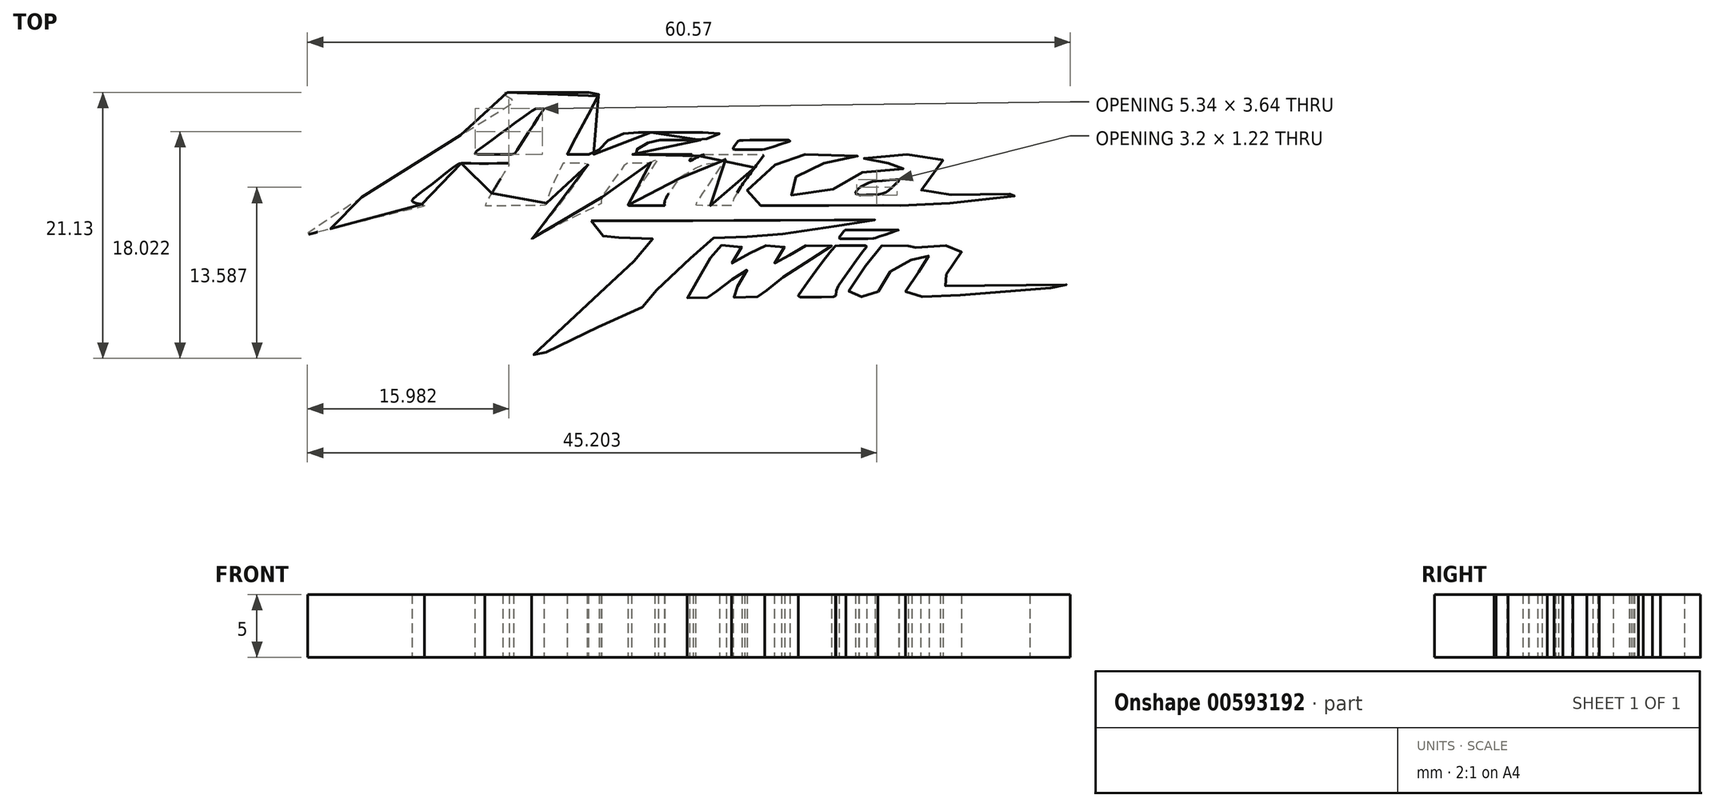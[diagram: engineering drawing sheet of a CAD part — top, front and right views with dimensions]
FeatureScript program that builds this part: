
annotation { "Feature Type Name" : "Feature", "Feature Type Description" : "" }
export const myFeature = defineFeature(function(context is Context, id is Id, definition is map)
    precondition{}
    {
        {
            var Q0;
            Q0=qCreatedBy(makeId("Top.planeOp"),FACE);
            var sketch = newSketch(context, id + "F0", { "sketchPlane" : qUnion([Q0])});
            skFitSpline(sketch, "E0", {"points": [v(-31.44, 20.71) * mm, v(-28.3, 20.77) * mm, v(-24.77, 20.79) * mm, v(-21.15, 20.83) * mm, v(-17.69, 20.85) * mm, v(-13.86, 20.87) * mm, v(-10.72, 20.85) * mm, v(-9.64, 20.77) * mm, v(-9.44, 20.67) * mm, v(-9.36, 20.45) * mm, v(-9.71, 19.84) * mm, v(-10.66, 17.85) * mm, v(-11.86, 15.37) * mm, v(-12.62, 13.83) * mm, v(-12.87, 13.46) * mm, v(-12.36, 13.66) * mm, v(-10.48, 14.38) * mm, v(-9.76, 14.62) * mm, v(-8.3, 14.67) * mm, v(-0.15, 14.62) * mm, v(8.5, 14.6) * mm, v(10.43, 14.62) * mm, v(10.86, 14.5) * mm, v(10.52, 14.24) * mm, v(9.13, 13.52) * mm, v(8.62, 13.24) * mm, v(9.3, 13.23) * mm, v(13.38, 13.2) * mm, v(17.6, 13.21) * mm, v(21.22, 13.2) * mm, v(22.36, 13.21) * mm, v(22.72, 13.17) * mm, v(22.9, 13.05) * mm, v(22.8, 12.92) * mm, v(22, 12.5) * mm, v(19.52, 11.38) * mm, v(19.17, 11.22) * mm, v(19.52, 11.18) * mm, v(21.42, 11.2) * mm, v(27.58, 11.15) * mm, v(35.7, 11.2) * mm, v(39.4, 11.2) * mm, v(39.96, 11.2) * mm, v(40.45, 11.02) * mm, v(41.07, 10.67) * mm, v(43.51, 8.93) * mm, v(43.88, 8.62) * mm, v(44.1, 8.35) * mm, v(44.07, 8.16) * mm, v(43.88, 7.78) * mm, v(43.2, 6.82) * mm, v(41.7, 4.75) * mm, v(41.4, 4.44) * mm, v(41.8, 4.44) * mm, v(46.51, 4.34) * mm, v(54.03, 4.15) * mm, v(62.87, 3.9) * mm, v(63.5, 3.86) * mm, v(63.75, 3.7) * mm, v(63.8, 3.5) * mm, v(63.56, 3.27) * mm, v(62.78, 3.02) * mm, v(61.33, 2.68) * mm, v(50.17, 0.51) * mm, v(48.29, 0.16) * mm, v(43.82, -0.7) * mm, v(41.17, -1.17) * mm, v(40.71, -1.31) * mm, v(40.3, -1.52) * mm, v(38.4, -2.7) * mm, v(38.08, -2.95) * mm, v(38.48, -2.96) * mm, v(42.95, -2.96) * mm, v(43.87, -3) * mm, v(44.42, -3.15) * mm, v(45.17, -3.73) * mm, v(47.66, -5.83) * mm, v(47.85, -6) * mm, v(47.88, -6.2) * mm, v(47.65, -6.53) * mm, v(45.18, -9.97) * mm, v(44.95, -10.32) * mm, v(45.44, -10.34) * mm, v(49.6, -10.42) * mm, v(60.85, -10.66) * mm, v(68.92, -10.88) * mm, v(69.35, -10.9) * mm, v(69.58, -11.06) * mm, v(69.63, -11.3) * mm, v(69.4, -11.5) * mm, v(68.72, -11.77) * mm, v(67.84, -11.94) * mm, v(61.37, -13.03) * mm, v(54.69, -13.9) * mm, v(46.25, -14.7) * mm, v(39.74, -15.1) * mm, v(35.06, -15.2) * mm, v(29.92, -15.28) * mm, v(24.8, -15.36) * mm, v(22.23, -15.43) * mm, v(14.78, -15.56) * mm, v(7.73, -15.76) * mm, v(1.76, -15.96) * mm, v(-0.16, -16.08) * mm, v(-1.23, -16.17) * mm, v(-1.7, -16.22) * mm, v(-2.2, -16.36) * mm, v(-3.15, -16.73) * mm, v(-5.36, -17.68) * mm, v(-8.55, -19) * mm, v(-11.16, -20.13) * mm, v(-15.96, -22.24) * mm, v(-19.22, -23.72) * mm, v(-24.73, -26.23) * mm, v(-29.57, -28.5) * mm, v(-31.83, -29.52) * mm, v(-33.6, -30.36) * mm, v(-33.79, -30.44) * mm, v(-33.93, -30.42) * mm, v(-34.06, -30.3) * mm, v(-34.08, -30.09) * mm, v(-33.96, -29.86) * mm, v(-33.08, -28.95) * mm, v(-30.44, -26.24) * mm, v(-27.52, -23.44) * mm, v(-24.82, -20.86) * mm, v(-21.12, -17.38) * mm, v(-17.92, -14.4) * mm, v(-14.38, -11.08) * mm, v(-11, -7.9) * mm, v(-9.75, -6.67) * mm, v(-9.62, -6.52) * mm, v(-9.85, -6.53) * mm, v(-10.86, -6.51) * mm, v(-10.98, -6.5) * mm, v(-11.63, -6.92) * mm, v(-11.95, -7.17) * mm, v(-12.1, -7.28) * mm, v(-12.24, -7.26) * mm, v(-12.64, -6.9) * mm, v(-15.8, -3.99) * mm, v(-16.66, -3.2) * mm, v(-16.75, -3.13) * mm, v(-16.94, -3.2) * mm, v(-19.02, -4.23) * mm, v(-21.54, -5.46) * mm, v(-26.34, -7.81) * mm, v(-30.32, -9.78) * mm, v(-31.48, -10.3) * mm, v(-31.67, -10.36) * mm, v(-31.85, -10.36) * mm, v(-31.94, -10.3) * mm, v(-32.02, -10.18) * mm, v(-31.91, -9.98) * mm, v(-31.16, -9.08) * mm, v(-27.72, -4.86) * mm, v(-25.69, -2.27) * mm, v(-25.03, -1.4) * mm, v(-24.98, -1.27) * mm, v(-25.27, -1.27) * mm, v(-30.34, -1.33) * mm, v(-34.83, -1.37) * mm, v(-35.61, -1.39) * mm, v(-35.8, -1.35) * mm, v(-35.92, -1.19) * mm, v(-35.92, -0.93) * mm, v(-35.79, -0.6) * mm, v(-35.04, 0.69) * mm, v(-33.92, 2.35) * mm, v(-32.9, 3.85) * mm, v(-31.97, 5.16) * mm, v(-31.97, 5.22) * mm, v(-32.3, 5.21) * mm, v(-34.88, 5.21) * mm, v(-34.96, 5.2) * mm, v(-35.2, 5.11) * mm, v(-36.44, 4.2) * mm, v(-38.05, 2.99) * mm, v(-38.72, 2.42) * mm, v(-38.81, 2.3) * mm, v(-38.79, 2.2) * mm, v(-38.64, 2.13) * mm, v(-38.37, 2) * mm, v(-36.75, 1.34) * mm, v(-36.2, 1.05) * mm, v(-35.96, 0.86) * mm, v(-35.85, 0.75) * mm, v(-35.93, 0.63) * mm, v(-36.35, 0.46) * mm, v(-37.36, 0.16) * mm, v(-39.12, -0.35) * mm, v(-42.53, -1.26) * mm, v(-47.35, -2.49) * mm, v(-52.88, -3.85) * mm, v(-58.58, -5.28) * mm, v(-64.61, -6.93) * mm, v(-67.43, -7.8) * mm, v(-67.74, -7.88) * mm, v(-68.03, -7.92) * mm, v(-68.31, -7.88) * mm, v(-68.5, -7.72) * mm, v(-68.5, -7.48) * mm, v(-68.17, -7.1) * mm, v(-67.4, -6.57) * mm, v(-64.48, -4.56) * mm, v(-61.76, -2.71) * mm, v(-58.36, -0.4) * mm, v(-55.05, 1.82) * mm, v(-52.23, 3.7) * mm, v(-49.26, 5.65) * mm, v(-46.62, 7.37) * mm, v(-43.48, 9.42) * mm, v(-40.62, 11.22) * mm, v(-37.84, 13) * mm, v(-34.36, 15.19) * mm, v(-31.23, 17.12) * mm, v(-30.7, 17.45) * mm, v(-30.59, 17.53) * mm, v(-30.7, 17.64) * mm, v(-31.88, 18.45) * mm, v(-33.47, 19.51) * mm, v(-34.2, 20.02) * mm, v(-34.3, 20.16) * mm, v(-34.33, 20.32) * mm, v(-34.21, 20.45) * mm, v(-33.86, 20.55) * mm, v(-33.08, 20.64) * mm, v(-32.38, 20.68) * mm, v(-31.44, 20.71) * mm]});
            skFitSpline(sketch, "E1", {"points": [v(-27.94, 18.83) * mm, v(-25.36, 18.85) * mm, v(-22.64, 18.83) * mm, v(-20.72, 18.82) * mm, v(-18.67, 18.83) * mm, v(-15.9, 18.83) * mm, v(-14.1, 18.83) * mm, v(-13.7, 18.83) * mm, v(-13.59, 18.81) * mm, v(-13.4, 18.65) * mm, v(-13.37, 18.58) * mm, v(-13.39, 18.45) * mm, v(-13.7, 17.85) * mm, v(-14.8, 15.8) * mm, v(-15.84, 13.94) * mm, v(-17.05, 11.71) * mm, v(-17.96, 9.93) * mm, v(-18.38, 9.15) * mm, v(-18.43, 9.04) * mm, v(-18.36, 8.98) * mm, v(-18.19, 8.98) * mm, v(-16.4, 8.98) * mm, v(-14.38, 9) * mm, v(-14.13, 9) * mm, v(-14, 9) * mm, v(-13.85, 9.16) * mm, v(-13.33, 9.76) * mm, v(-12.75, 10.5) * mm, v(-12.45, 10.91) * mm, v(-12.36, 11.02) * mm, v(-12.14, 11.15) * mm, v(-11.18, 11.59) * mm, v(-10.62, 11.83) * mm, v(-9.52, 12.26) * mm, v(-9.14, 12.38) * mm, v(-8.8, 12.46) * mm, v(-8.18, 12.48) * mm, v(-6.37, 12.48) * mm, v(-3.07, 12.5) * mm, v(0.47, 12.48) * mm, v(4, 12.5) * mm, v(5.57, 12.5) * mm, v(5.7, 12.47) * mm, v(5.77, 12.4) * mm, v(5.78, 12.33) * mm, v(5.63, 12.27) * mm, v(5.55, 12.22) * mm, v(4.72, 11.87) * mm, v(3.96, 11.55) * mm, v(3.4, 11.36) * mm, v(3.14, 11.28) * mm, v(2.72, 11.26) * mm, v(1.7, 11.25) * mm, v(-1.97, 11.24) * mm, v(-4.14, 11.26) * mm, v(-4.41, 11.24) * mm, v(-4.77, 11.17) * mm, v(-5.2, 10.98) * mm, v(-5.83, 10.72) * mm, v(-6.38, 10.48) * mm, v(-6.7, 10.32) * mm, v(-7.08, 10.03) * mm, v(-7.67, 9.55) * mm, v(-8.12, 9.15) * mm, v(-8.16, 9.05) * mm, v(-8.07, 8.98) * mm, v(-7.9, 9) * mm, v(-5.92, 9) * mm, v(-2.75, 8.97) * mm, v(0.26, 8.98) * mm, v(1.36, 8.99) * mm, v(1.5, 8.97) * mm, v(1.57, 8.94) * mm, v(1.6, 8.87) * mm, v(1.57, 8.8) * mm, v(1.47, 8.68) * mm, v(1.1, 8.12) * mm, v(1.03, 8.03) * mm, v(1.1, 7.95) * mm, v(1.2, 7.98) * mm, v(1.46, 8.12) * mm, v(2.51, 8.65) * mm, v(3.07, 8.87) * mm, v(3.35, 8.95) * mm, v(3.77, 8.97) * mm, v(5.54, 8.99) * mm, v(7.3, 8.97) * mm, v(9.54, 8.98) * mm, v(12.54, 8.99) * mm, v(12.68, 8.98) * mm, v(12.77, 8.95) * mm, v(12.82, 8.88) * mm, v(12.8, 8.83) * mm, v(12.7, 8.7) * mm, v(12.39, 8.3) * mm, v(11.56, 7.18) * mm, v(10.72, 6) * mm, v(9.85, 4.83) * mm, v(9.03, 3.65) * mm, v(8.33, 2.51) * mm, v(8.12, 2.16) * mm, v(7.97, 1.78) * mm, v(7.9, 1.55) * mm, v(7.9, 1.26) * mm, v(7.92, 1.1) * mm, v(7.96, 1.01) * mm, v(7.95, 0.92) * mm, v(7.88, 0.85) * mm, v(7.64, 0.85) * mm, v(7.26, 0.86) * mm, v(5.58, 0.85) * mm, v(4, 0.85) * mm, v(2.88, 0.84) * mm, v(2.23, 0.83) * mm, v(2.14, 0.87) * mm, v(2.05, 0.92) * mm, v(2, 1) * mm, v(2, 1.11) * mm, v(2.11, 1.26) * mm, v(2.32, 1.6) * mm, v(3.29, 3.02) * mm, v(4.07, 4.21) * mm, v(4.93, 5.49) * mm, v(5.7, 6.66) * mm, v(6.27, 7.5) * mm, v(6.62, 8.04) * mm, v(6.77, 8.25) * mm, v(6.84, 8.35) * mm, v(6.8, 8.39) * mm, v(6.75, 8.36) * mm, v(6.6, 8.3) * mm, v(6.12, 8.06) * mm, v(5.7, 7.86) * mm, v(5.39, 7.68) * mm, v(5.17, 7.57) * mm, v(4.7, 7.51) * mm, v(4.02, 7.45) * mm, v(3.55, 7.4) * mm, v(3.34, 7.36) * mm, v(3.18, 7.3) * mm, v(2.6, 7.04) * mm, v(1.12, 6.3) * mm, v(-0.07, 5.6) * mm, v(-0.36, 5.41) * mm, v(-0.58, 5.19) * mm, v(-0.91, 4.83) * mm, v(-1.73, 3.65) * mm, v(-2.5, 2.48) * mm, v(-2.83, 1.87) * mm, v(-2.94, 1.49) * mm, v(-2.97, 1.2) * mm, v(-2.94, 0.93) * mm, v(-2.93, 0.86) * mm, v(-3.01, 0.83) * mm, v(-3.3, 0.84) * mm, v(-4.13, 0.84) * mm, v(-6.48, 0.84) * mm, v(-8.4, 0.84) * mm, v(-8.54, 0.85) * mm, v(-8.67, 0.9) * mm, v(-8.74, 0.95) * mm, v(-8.78, 1.04) * mm, v(-8.74, 1.15) * mm, v(-8.6, 1.33) * mm, v(-8.25, 1.87) * mm, v(-7.37, 3.17) * mm, v(-6.3, 4.76) * mm, v(-5.43, 6.05) * mm, v(-4.42, 7.53) * mm, v(-4.17, 7.86) * mm, v(-3.95, 8.14) * mm, v(-3.91, 8.2) * mm, v(-3.93, 8.22) * mm, v(-3.98, 8.25) * mm, v(-4.12, 8.19) * mm, v(-4.58, 7.97) * mm, v(-4.8, 7.86) * mm, v(-5.04, 7.75) * mm, v(-5.15, 7.68) * mm, v(-5.28, 7.57) * mm, v(-5.41, 7.57) * mm, v(-6.5, 7.58) * mm, v(-7.44, 7.6) * mm, v(-8.45, 7.58) * mm, v(-8.72, 7.59) * mm, v(-8.86, 7.58) * mm, v(-9.02, 7.53) * mm, v(-9.2, 7.4) * mm, v(-9.4, 7.17) * mm, v(-10.12, 6.14) * mm, v(-10.87, 5.13) * mm, v(-12.03, 3.51) * mm, v(-12.67, 2.61) * mm, v(-12.94, 2.1) * mm, v(-13, 1.78) * mm, v(-12.98, 1.39) * mm, v(-12.98, 1.24) * mm, v(-12.98, 1.18) * mm, v(-13.05, 1.12) * mm, v(-13.57, 0.85) * mm, v(-16.05, -0.34) * mm, v(-18.68, -1.62) * mm, v(-21.07, -2.85) * mm, v(-23.2, -4.06) * mm, v(-23.86, -4.42) * mm, v(-23.99, -4.46) * mm, v(-23.97, -4.38) * mm, v(-23.9, -4.3) * mm, v(-23.55, -3.86) * mm, v(-22.4, -2.47) * mm, v(-21.58, -1.48) * mm, v(-21.03, -0.75) * mm, v(-20.06, 0.46) * mm, v(-19.46, 1.23) * mm, v(-17.66, 3.63) * mm, v(-15.85, 6.13) * mm, v(-15.14, 7.15) * mm, v(-15.08, 7.24) * mm, v(-15.1, 7.37) * mm, v(-15.22, 7.48) * mm, v(-15.39, 7.55) * mm, v(-15.54, 7.59) * mm, v(-16.37, 7.58) * mm, v(-18.12, 7.59) * mm, v(-18.98, 7.59) * mm, v(-19.06, 7.6) * mm, v(-19.12, 7.57) * mm, v(-19.19, 7.46) * mm, v(-19.71, 6.32) * mm, v(-20.6, 4.39) * mm, v(-21.2, 3) * mm, v(-21.35, 2.6) * mm, v(-21.5, 2.03) * mm, v(-21.7, 1.2) * mm, v(-21.75, 1.05) * mm, v(-21.8, 0.96) * mm, v(-21.91, 0.89) * mm, v(-22.11, 0.86) * mm, v(-22.6, 0.87) * mm, v(-25.77, 0.85) * mm, v(-28.27, 0.82) * mm, v(-30.4, 0.78) * mm, v(-31.24, 0.76) * mm, v(-31.37, 0.78) * mm, v(-31.45, 0.84) * mm, v(-31.48, 0.93) * mm, v(-31.44, 1.05) * mm, v(-31.24, 1.34) * mm, v(-30.56, 2.5) * mm, v(-30.22, 3.09) * mm, v(-29.67, 4.03) * mm, v(-29.06, 4.98) * mm, v(-28.3, 6.24) * mm, v(-27.74, 7.1) * mm, v(-27.63, 7.3) * mm, v(-27.6, 7.44) * mm, v(-27.66, 7.53) * mm, v(-27.78, 7.57) * mm, v(-28.8, 7.57) * mm, v(-32.18, 7.55) * mm, v(-34.64, 7.59) * mm, v(-35.2, 7.6) * mm, v(-35.48, 7.55) * mm, v(-35.8, 7.42) * mm, v(-36.13, 7.21) * mm, v(-36.46, 6.95) * mm, v(-37.18, 6.43) * mm, v(-39.8, 4.34) * mm, v(-41.94, 2.73) * mm, v(-42.38, 2.35) * mm, v(-42.88, 1.92) * mm, v(-43.03, 1.74) * mm, v(-43.06, 1.59) * mm, v(-42.98, 1.45) * mm, v(-42.76, 1.34) * mm, v(-41.95, 1.15) * mm, v(-41.37, 1.02) * mm, v(-41.17, 0.92) * mm, v(-41.08, 0.85) * mm, v(-41.08, 0.78) * mm, v(-41.16, 0.73) * mm, v(-41.47, 0.67) * mm, v(-41.8, 0.57) * mm, v(-44.01, 0.07) * mm, v(-45.43, -0.27) * mm, v(-48.03, -0.9) * mm, v(-51.88, -1.85) * mm, v(-54.82, -2.56) * mm, v(-58.1, -3.36) * mm, v(-59.13, -3.63) * mm, v(-59.46, -3.7) * mm, v(-59.64, -3.68) * mm, v(-59.65, -3.61) * mm, v(-59.58, -3.5) * mm, v(-59.4, -3.34) * mm, v(-58.34, -2.59) * mm, v(-56.94, -1.67) * mm, v(-54.92, -0.34) * mm, v(-53.9, 0.34) * mm, v(-51.67, 1.76) * mm, v(-49.53, 3.14) * mm, v(-48.87, 3.58) * mm, v(-48.73, 3.67) * mm, v(-47.04, 4.75) * mm, v(-44.1, 6.6) * mm, v(-41.55, 8.22) * mm, v(-38.39, 10.15) * mm, v(-35.9, 11.7) * mm, v(-33.5, 13.18) * mm, v(-30.87, 14.8) * mm, v(-27.86, 16.62) * mm, v(-26.98, 17.22) * mm, v(-26.93, 17.35) * mm, v(-26.94, 17.46) * mm, v(-27.02, 17.57) * mm, v(-27.47, 17.84) * mm, v(-27.98, 18.15) * mm, v(-28.6, 18.54) * mm, v(-28.65, 18.63) * mm, v(-28.66, 18.74) * mm, v(-28.59, 18.83) * mm, v(-28.36, 18.84) * mm, v(-27.94, 18.83) * mm]});
            skFitSpline(sketch, "E2", {"points": [v(-22.35, 15.82) * mm, v(-22.84, 15.12) * mm, v(-23.43, 14.18) * mm, v(-24.2, 13.02) * mm, v(-24.91, 11.9) * mm, v(-26, 10.2) * mm, v(-26.5, 9.37) * mm, v(-26.57, 9.25) * mm, v(-26.7, 9.13) * mm, v(-26.97, 9) * mm, v(-27.15, 8.98) * mm, v(-27.78, 8.98) * mm, v(-30.38, 8.98) * mm, v(-32.52, 8.99) * mm, v(-32.62, 8.99) * mm, v(-32.84, 9) * mm, v(-32.96, 9.05) * mm, v(-33.05, 9.11) * mm, v(-33.07, 9.23) * mm, v(-33, 9.36) * mm, v(-32.83, 9.5) * mm, v(-32.07, 10.06) * mm, v(-30.65, 11.06) * mm, v(-29.08, 12.22) * mm, v(-28.27, 12.82) * mm, v(-26.87, 13.82) * mm, v(-25.71, 14.67) * mm, v(-24.21, 15.76) * mm, v(-23.77, 16.09) * mm, v(-23.6, 16.2) * mm, v(-23.35, 16.27) * mm, v(-23.1, 16.3) * mm, v(-22.62, 16.3) * mm, v(-22.22, 16.32) * mm, v(-22.13, 16.28) * mm, v(-22.11, 16.21) * mm, v(-22.15, 16.15) * mm, v(-22.25, 16) * mm, v(-22.35, 15.82) * mm]});
            skFitSpline(sketch, "E3", {"points": [v(12, 11.25) * mm, v(14.22, 11.25) * mm, v(16.62, 11.24) * mm, v(16.78, 11.24) * mm, v(16.86, 11.21) * mm, v(16.96, 11.13) * mm, v(16.95, 11.09) * mm, v(16.84, 11.03) * mm, v(16.26, 10.83) * mm, v(14.13, 10.16) * mm, v(13.26, 9.87) * mm, v(13.01, 9.8) * mm, v(12.88, 9.79) * mm, v(12.62, 9.75) * mm, v(12, 9.74) * mm, v(9.53, 9.74) * mm, v(8.25, 9.74) * mm, v(8.1, 9.75) * mm, v(8, 9.8) * mm, v(7.93, 9.9) * mm, v(7.96, 10) * mm, v(8.08, 10.19) * mm, v(8.3, 10.52) * mm, v(8.66, 11.04) * mm, v(8.75, 11.14) * mm, v(8.92, 11.2) * mm, v(9.11, 11.22) * mm, v(9.68, 11.23) * mm, v(12, 11.25) * mm]});
            skFitSpline(sketch, "E4", {"points": [v(19.36, 8.99) * mm, v(22.68, 8.97) * mm, v(26.98, 8.98) * mm, v(27.74, 8.98) * mm, v(27.87, 8.95) * mm, v(27.9, 8.9) * mm, v(27.9, 8.85) * mm, v(27.81, 8.79) * mm, v(26.72, 8.05) * mm, v(26.31, 7.8) * mm, v(26.14, 7.7) * mm, v(25.95, 7.64) * mm, v(25.68, 7.6) * mm, v(25.22, 7.58) * mm, v(23.34, 7.58) * mm, v(22.34, 7.58) * mm, v(22.07, 7.58) * mm, v(21.9, 7.56) * mm, v(21.57, 7.43) * mm, v(20.7, 7.11) * mm, v(19.5, 6.6) * mm, v(19.23, 6.46) * mm, v(18.91, 6.25) * mm, v(18.35, 5.78) * mm, v(16.43, 4.07) * mm, v(15.81, 3.42) * mm, v(15.68, 3.27) * mm, v(15.64, 3.16) * mm, v(15.67, 3) * mm, v(15.77, 2.85) * mm, v(16.02, 2.67) * mm, v(16.3, 2.56) * mm, v(16.65, 2.52) * mm, v(17.73, 2.53) * mm, v(21.55, 2.52) * mm, v(22.6, 2.53) * mm, v(22.94, 2.53) * mm, v(23, 2.53) * mm, v(23.05, 2.6) * mm, v(23.41, 3.02) * mm, v(23.63, 3.26) * mm, v(24.59, 4.23) * mm, v(25.3, 4.9) * mm, v(25.69, 5.2) * mm, v(25.97, 5.35) * mm, v(26.75, 5.64) * mm, v(27.39, 5.85) * mm, v(28.23, 6.08) * mm, v(28.93, 6.15) * mm, v(29.7, 6.23) * mm, v(31.7, 6.4) * mm, v(33.63, 6.54) * mm, v(34.2, 6.6) * mm, v(34.7, 6.66) * mm, v(35.26, 6.83) * mm, v(35.67, 7.05) * mm, v(36.07, 7.23) * mm, v(36.27, 7.4) * mm, v(36.3, 7.48) * mm, v(36.3, 7.54) * mm, v(36.25, 7.57) * mm, v(36.1, 7.57) * mm, v(34.31, 7.56) * mm, v(32.6, 7.56) * mm, v(30.43, 7.56) * mm, v(28.46, 7.56) * mm, v(28.03, 7.55) * mm, v(27.98, 7.56) * mm, v(27.91, 7.6) * mm, v(27.86, 7.67) * mm, v(27.85, 7.73) * mm, v(27.9, 7.8) * mm, v(28.04, 7.9) * mm, v(28.89, 8.5) * mm, v(29.46, 8.87) * mm, v(29.62, 8.94) * mm, v(29.72, 8.98) * mm, v(29.84, 8.99) * mm, v(30.41, 9) * mm, v(32.93, 9) * mm, v(35.39, 8.99) * mm, v(38.86, 8.99) * mm, v(39.63, 8.98) * mm, v(39.87, 8.97) * mm, v(40.04, 8.93) * mm, v(40.22, 8.87) * mm, v(40.42, 8.75) * mm, v(41.05, 8.3) * mm, v(41.22, 8.16) * mm, v(41.28, 8.07) * mm, v(41.3, 7.97) * mm, v(41.27, 7.87) * mm, v(41.14, 7.68) * mm, v(41.01, 7.5) * mm, v(40.1, 6.26) * mm, v(39.1, 4.97) * mm, v(38.1, 3.7) * mm, v(37.82, 3.3) * mm, v(37.74, 3.21) * mm, v(37.71, 3.11) * mm, v(37.74, 3.03) * mm, v(37.83, 2.93) * mm, v(38.07, 2.8) * mm, v(38.36, 2.63) * mm, v(38.56, 2.56) * mm, v(38.7, 2.54) * mm, v(39.3, 2.56) * mm, v(41.81, 2.58) * mm, v(44.71, 2.63) * mm, v(47.11, 2.67) * mm, v(49.35, 2.7) * mm, v(51.41, 2.72) * mm, v(52.93, 2.75) * mm, v(54.17, 2.77) * mm, v(54.89, 2.79) * mm, v(54.96, 2.8) * mm, v(55.02, 2.78) * mm, v(55.05, 2.74) * mm, v(55.03, 2.71) * mm, v(54.96, 2.68) * mm, v(54.82, 2.66) * mm, v(53.2, 2.43) * mm, v(51.02, 2.17) * mm, v(48.66, 1.9) * mm, v(45.26, 1.54) * mm, v(41.9, 1.17) * mm, v(39.22, 0.86) * mm, v(38.78, 0.84) * mm, v(36.51, 0.83) * mm, v(35.17, 0.83) * mm, v(34.5, 0.86) * mm, v(34.22, 0.9) * mm, v(34.05, 0.96) * mm, v(33.78, 1.18) * mm, v(33.61, 1.38) * mm, v(33.52, 1.52) * mm, v(33.42, 1.69) * mm, v(33.38, 1.76) * mm, v(33.36, 1.75) * mm, v(33.27, 1.66) * mm, v(32.95, 1.44) * mm, v(32.42, 1.15) * mm, v(32.03, 0.98) * mm, v(31.5, 0.89) * mm, v(30.58, 0.84) * mm, v(28.38, 0.84) * mm, v(25.63, 0.85) * mm, v(23.37, 0.85) * mm, v(19.81, 0.85) * mm, v(16.57, 0.85) * mm, v(13.2, 0.84) * mm, v(12.09, 0.83) * mm, v(11.79, 0.85) * mm, v(11.35, 1) * mm, v(10.86, 1.32) * mm, v(10.16, 2.03) * mm, v(9.82, 2.45) * mm, v(9.75, 2.63) * mm, v(9.75, 2.76) * mm, v(9.81, 2.9) * mm, v(9.97, 3.08) * mm, v(10.5, 3.63) * mm, v(11.11, 4.23) * mm, v(11.88, 4.94) * mm, v(13, 5.95) * mm, v(14.06, 6.9) * mm, v(14.34, 7.11) * mm, v(14.56, 7.3) * mm, v(15.03, 7.59) * mm, v(15.46, 7.77) * mm, v(16.45, 8.18) * mm, v(17.81, 8.69) * mm, v(18.25, 8.85) * mm, v(18.6, 8.95) * mm, v(18.93, 8.99) * mm, v(19.36, 8.99) * mm]});
            skFitSpline(sketch, "E5", {"points": [v(30.67, 4.75) * mm, v(32.06, 4.83) * mm, v(33.57, 4.98) * mm, v(34.1, 5) * mm, v(34.25, 4.98) * mm, v(34.3, 4.94) * mm, v(34.3, 4.86) * mm, v(34.18, 4.73) * mm, v(33.6, 4.16) * mm, v(32.93, 3.51) * mm, v(32.56, 3.19) * mm, v(32.18, 2.95) * mm, v(31.7, 2.76) * mm, v(31.22, 2.65) * mm, v(30.5, 2.56) * mm, v(28.92, 2.54) * mm, v(27.99, 2.53) * mm, v(27.72, 2.58) * mm, v(27.49, 2.74) * mm, v(27.38, 2.83) * mm, v(27.35, 2.9) * mm, v(27.4, 3.02) * mm, v(27.57, 3.28) * mm, v(27.68, 3.42) * mm, v(27.96, 3.64) * mm, v(28.47, 3.97) * mm, v(29.04, 4.3) * mm, v(29.6, 4.54) * mm, v(30.1, 4.68) * mm, v(30.67, 4.75) * mm]});
            skFitSpline(sketch, "E6", {"points": [v(-14.6, -1.57) * mm, v(-11.2, -1.57) * mm, v(-8.48, -1.56) * mm, v(-4.15, -1.55) * mm, v(-0.76, -1.54) * mm, v(2.28, -1.52) * mm, v(4.75, -1.5) * mm, v(6.58, -1.5) * mm, v(8.88, -1.5) * mm, v(11.94, -1.5) * mm, v(14.7, -1.47) * mm, v(17.8, -1.44) * mm, v(22.1, -1.44) * mm, v(25.9, -1.42) * mm, v(29.15, -1.42) * mm, v(29.99, -1.41) * mm, v(30.42, -1.4) * mm, v(30.5, -1.42) * mm, v(30.5, -1.45) * mm, v(30.4, -1.48) * mm, v(28.76, -1.77) * mm, v(25.05, -2.3) * mm, v(21.95, -2.78) * mm, v(17.9, -3.34) * mm, v(13.88, -3.92) * mm, v(12.93, -4.08) * mm, v(12.07, -4.13) * mm, v(10.14, -4.11) * mm, v(8.64, -4.14) * mm, v(5.74, -4.19) * mm, v(5.16, -4.21) * mm, v(4.9, -4.26) * mm, v(4.63, -4.38) * mm, v(4.25, -4.64) * mm, v(3.5, -5.28) * mm, v(2.2, -6.52) * mm, v(0.46, -8.22) * mm, v(-1.37, -9.96) * mm, v(-3.6, -12.02) * mm, v(-5.55, -13.84) * mm, v(-5.8, -14.14) * mm, v(-6.04, -14.49) * mm, v(-6.16, -14.84) * mm, v(-6.29, -15.13) * mm, v(-6.33, -15.2) * mm, v(-6.42, -15.26) * mm, v(-6.73, -15.42) * mm, v(-10.19, -16.97) * mm, v(-13.51, -18.47) * mm, v(-17.5, -20.35) * mm, v(-21.58, -22.33) * mm, v(-23.28, -23.15) * mm, v(-23.75, -23.37) * mm, v(-23.85, -23.4) * mm, v(-24, -23.4) * mm, v(-24.06, -23.38) * mm, v(-24.08, -23.3) * mm, v(-24.05, -23.2) * mm, v(-23.92, -23.03) * mm, v(-23.24, -22.4) * mm, v(-21.57, -20.8) * mm, v(-20.09, -19.4) * mm, v(-17.6, -17.07) * mm, v(-15.2, -14.85) * mm, v(-13.02, -12.8) * mm, v(-10.94, -10.93) * mm, v(-8.92, -9.02) * mm, v(-6.32, -6.58) * mm, v(-4.75, -5.1) * mm, v(-4.58, -4.88) * mm, v(-4.54, -4.78) * mm, v(-4.56, -4.66) * mm, v(-4.85, -4.45) * mm, v(-5.14, -4.28) * mm, v(-5.25, -4.23) * mm, v(-5.49, -4.24) * mm, v(-7, -4.24) * mm, v(-10.43, -4.22) * mm, v(-11.54, -4.22) * mm, v(-11.66, -4.23) * mm, v(-11.73, -4.25) * mm, v(-11.84, -4.36) * mm, v(-11.98, -4.47) * mm, v(-12.05, -4.5) * mm, v(-12.1, -4.49) * mm, v(-12.23, -4.4) * mm, v(-12.56, -4.1) * mm, v(-14.16, -2.73) * mm, v(-15.13, -1.84) * mm, v(-15.2, -1.76) * mm, v(-15.23, -1.66) * mm, v(-15.19, -1.6) * mm, v(-15.1, -1.56) * mm, v(-14.6, -1.57) * mm]});
            skFitSpline(sketch, "E7", {"points": [v(6.07, -5.46) * mm, v(8.68, -5.48) * mm, v(9.15, -5.5) * mm, v(9.27, -5.5) * mm, v(9.33, -5.53) * mm, v(9.36, -5.6) * mm, v(9.32, -5.69) * mm, v(9.2, -5.9) * mm, v(8.52, -6.99) * mm, v(8.03, -7.79) * mm, v(7.8, -8.15) * mm, v(7.77, -8.25) * mm, v(7.78, -8.35) * mm, v(7.86, -8.41) * mm, v(8, -8.35) * mm, v(8.57, -7.98) * mm, v(9.33, -7.52) * mm, v(10.97, -6.48) * mm, v(11.65, -6.02) * mm, v(12.27, -5.64) * mm, v(12.43, -5.55) * mm, v(12.66, -5.5) * mm, v(13.2, -5.47) * mm, v(14, -5.48) * mm, v(15.85, -5.48) * mm, v(16.05, -5.52) * mm, v(16.1, -5.56) * mm, v(16.14, -5.64) * mm, v(16.06, -5.78) * mm, v(15.87, -6.06) * mm, v(15.23, -7.14) * mm, v(14.78, -7.84) * mm, v(14.57, -8.2) * mm, v(14.51, -8.3) * mm, v(14.52, -8.4) * mm, v(14.6, -8.43) * mm, v(14.8, -8.31) * mm, v(15.52, -7.85) * mm, v(16.5, -7.26) * mm, v(17.29, -6.78) * mm, v(18.2, -6.26) * mm, v(19, -5.76) * mm, v(19.28, -5.58) * mm, v(19.41, -5.51) * mm, v(19.6, -5.48) * mm, v(19.84, -5.48) * mm, v(23.1, -5.47) * mm, v(23.46, -5.48) * mm, v(23.52, -5.48) * mm, v(23.56, -5.53) * mm, v(23.5, -5.58) * mm, v(23.22, -5.77) * mm, v(22.43, -6.3) * mm, v(20.83, -7.31) * mm, v(19.24, -8.32) * mm, v(17.72, -9.29) * mm, v(15.52, -10.77) * mm, v(14.27, -11.65) * mm, v(13.88, -11.95) * mm, v(13.56, -12.26) * mm, v(13.28, -12.57) * mm, v(13.1, -12.83) * mm, v(12.97, -13.1) * mm, v(12.94, -13.32) * mm, v(12.93, -13.51) * mm, v(12.93, -13.56) * mm, v(12.88, -13.58) * mm, v(12.76, -13.6) * mm, v(11.73, -13.6) * mm, v(10.8, -13.63) * mm, v(9.54, -13.7) * mm, v(8.3, -13.72) * mm, v(7.96, -13.73) * mm, v(7.82, -13.7) * mm, v(7.72, -13.65) * mm, v(7.7, -13.58) * mm, v(7.71, -13.46) * mm, v(7.93, -13.07) * mm, v(8.34, -12.42) * mm, v(8.9, -11.42) * mm, v(9.36, -10.66) * mm, v(9.67, -10.16) * mm, v(9.96, -9.7) * mm, v(10.14, -9.4) * mm, v(10.18, -9.35) * mm, v(10.18, -9.32) * mm, v(10.15, -9.34) * mm, v(10.01, -9.41) * mm, v(9.36, -9.84) * mm, v(8.5, -10.42) * mm, v(7.48, -11.11) * mm, v(7, -11.48) * mm, v(6.18, -12.06) * mm, v(5.68, -12.42) * mm, v(5.4, -12.66) * mm, v(5.26, -12.88) * mm, v(5.14, -13.05) * mm, v(5.02, -13.34) * mm, v(4.95, -13.55) * mm, v(4.92, -13.66) * mm, v(4.86, -13.69) * mm, v(4.66, -13.7) * mm, v(3.26, -13.77) * mm, v(2.09, -13.86) * mm, v(1, -13.93) * mm, v(0.85, -13.91) * mm, v(0.75, -13.88) * mm, v(0.68, -13.81) * mm, v(0.66, -13.71) * mm, v(0.72, -13.57) * mm, v(0.86, -13.3) * mm, v(1.6, -12.07) * mm, v(2.29, -10.93) * mm, v(2.84, -10) * mm, v(3.3, -9.2) * mm, v(4.04, -7.98) * mm, v(4.69, -6.95) * mm, v(5.22, -6.06) * mm, v(5.58, -5.5) * mm, v(5.66, -5.47) * mm, v(5.84, -5.45) * mm, v(6.07, -5.46) * mm]});
            skFitSpline(sketch, "E8", {"points": [v(27.89, -3.02) * mm, v(30.66, -3.01) * mm, v(33.29, -3.01) * mm, v(34.05, -2.99) * mm, v(34.21, -3) * mm, v(34.21, -3.03) * mm, v(33.93, -3.12) * mm, v(32.8, -3.53) * mm, v(31.45, -3.98) * mm, v(30.54, -4.3) * mm, v(30.41, -4.35) * mm, v(30.27, -4.37) * mm, v(28.54, -4.4) * mm, v(26.16, -4.4) * mm, v(24.9, -4.4) * mm, v(24.83, -4.36) * mm, v(24.78, -4.29) * mm, v(24.81, -4.16) * mm, v(25.28, -3.56) * mm, v(25.66, -3.08) * mm, v(25.73, -3.02) * mm, v(25.8, -3) * mm, v(27.89, -3.02) * mm]});
            skFitSpline(sketch, "E9", {"points": [v(24.8, -5.5) * mm, v(28.52, -5.5) * mm, v(28.86, -5.5) * mm, v(29.01, -5.5) * mm, v(29.1, -5.54) * mm, v(29.14, -5.61) * mm, v(29.1, -5.7) * mm, v(28.82, -6.05) * mm, v(27.83, -7.4) * mm, v(26.59, -9.11) * mm, v(25.28, -10.96) * mm, v(24.71, -11.84) * mm, v(24.47, -12.25) * mm, v(24.3, -12.64) * mm, v(24.2, -12.98) * mm, v(24.23, -13.42) * mm, v(24.23, -13.54) * mm, v(24.23, -13.59) * mm, v(24.13, -13.6) * mm, v(22.42, -13.65) * mm, v(19.82, -13.68) * mm, v(18.58, -13.69) * mm, v(18.4, -13.66) * mm, v(18.33, -13.6) * mm, v(18.27, -13.5) * mm, v(18.3, -13.4) * mm, v(18.44, -13.2) * mm, v(19.41, -11.83) * mm, v(19.98, -11) * mm, v(21.08, -9.54) * mm, v(22.16, -8.03) * mm, v(23.26, -6.62) * mm, v(23.92, -5.86) * mm, v(24.17, -5.57) * mm, v(24.22, -5.5) * mm, v(24.3, -5.5) * mm, v(24.8, -5.5) * mm]});
            skFitSpline(sketch, "E10", {"points": [v(31.53, -5.5) * mm, v(33.25, -5.51) * mm, v(34.88, -5.5) * mm, v(35.52, -5.5) * mm, v(35.65, -5.5) * mm, v(35.77, -5.56) * mm, v(35.77, -5.62) * mm, v(35.68, -5.77) * mm, v(35.5, -6) * mm, v(35.4, -6.14) * mm, v(35.4, -6.2) * mm, v(35.44, -6.28) * mm, v(35.57, -6.25) * mm, v(35.9, -6.15) * mm, v(37.28, -5.67) * mm, v(37.62, -5.57) * mm, v(37.93, -5.51) * mm, v(38.46, -5.5) * mm, v(41.56, -5.5) * mm, v(42.63, -5.5) * mm, v(42.8, -5.51) * mm, v(43, -5.57) * mm, v(43.4, -5.86) * mm, v(44.09, -6.33) * mm, v(44.18, -6.43) * mm, v(44.22, -6.53) * mm, v(44.16, -6.65) * mm, v(43.75, -7.23) * mm, v(43.12, -8.14) * mm, v(42.08, -9.63) * mm, v(41.22, -10.8) * mm, v(40.87, -11.26) * mm, v(40.81, -11.36) * mm, v(40.83, -11.47) * mm, v(40.95, -11.6) * mm, v(41.2, -11.76) * mm, v(41.45, -11.87) * mm, v(41.79, -11.91) * mm, v(43.11, -11.9) * mm, v(46.35, -11.87) * mm, v(49.15, -11.83) * mm, v(51.56, -11.8) * mm, v(54.45, -11.79) * mm, v(56.8, -11.76) * mm, v(59.52, -11.7) * mm, v(61.18, -11.72) * mm, v(61.37, -11.73) * mm, v(61.44, -11.76) * mm, v(61.48, -11.8) * mm, v(61.46, -11.86) * mm, v(61.37, -11.91) * mm, v(61.07, -11.97) * mm, v(58.26, -12.25) * mm, v(55.58, -12.47) * mm, v(52.1, -12.74) * mm, v(48.76, -12.99) * mm, v(45.73, -13.22) * mm, v(42.7, -13.44) * mm, v(40.52, -13.6) * mm, v(39.03, -13.61) * mm, v(36.88, -13.6) * mm, v(36.7, -13.58) * mm, v(36.32, -13.48) * mm, v(35.7, -13.2) * mm, v(35.38, -13.01) * mm, v(35.32, -12.9) * mm, v(35.3, -12.8) * mm, v(35.38, -12.64) * mm, v(35.61, -12.3) * mm, v(36.07, -11.65) * mm, v(36.68, -10.79) * mm, v(37.42, -9.7) * mm, v(37.97, -8.93) * mm, v(38.58, -8.04) * mm, v(38.93, -7.57) * mm, v(39.04, -7.41) * mm, v(39.08, -7.28) * mm, v(39, -7.14) * mm, v(38.75, -7.06) * mm, v(38.34, -7.04) * mm, v(38, -7.02) * mm, v(37.72, -7.07) * mm, v(37.3, -7.26) * mm, v(36.37, -7.7) * mm, v(34.66, -8.42) * mm, v(33.8, -8.83) * mm, v(33.48, -9.02) * mm, v(33.25, -9.23) * mm, v(32.9, -9.63) * mm, v(32.06, -10.82) * mm, v(31.37, -11.84) * mm, v(31.1, -12.26) * mm, v(31, -12.56) * mm, v(30.96, -12.87) * mm, v(30.95, -13.3) * mm, v(30.94, -13.5) * mm, v(30.89, -13.57) * mm, v(30.79, -13.64) * mm, v(30.65, -13.66) * mm, v(29.9, -13.65) * mm, v(27.24, -13.66) * mm, v(26.11, -13.66) * mm, v(25.98, -13.64) * mm, v(25.88, -13.57) * mm, v(25.85, -13.47) * mm, v(25.9, -13.33) * mm, v(26.06, -13.08) * mm, v(26.73, -12.1) * mm, v(27.2, -11.4) * mm, v(28.14, -9.97) * mm, v(29.05, -8.62) * mm, v(30.39, -6.6) * mm, v(30.98, -5.7) * mm, v(31.1, -5.57) * mm, v(31.26, -5.53) * mm, v(31.53, -5.5) * mm]});
            skSolve(sketch);
        }
        {
            var Q0;
            Q0=makeQuery(id+"F0.imprint","IMPRINT",FACE,{"disambiguationData":[TD([[makeQuery(id+"F0.imprint","IMPRINT",EDGE,{"derivedFrom":sQuery(id+"F0.wireOp",EDGE,"E1")}),-1.0]])]});
            var Q1;
            Q1=makeQuery(id+"F0.imprint","IMPRINT",FACE,{"disambiguationData":[TD([[makeQuery(id+"F0.imprint","IMPRINT",EDGE,{"derivedFrom":sQuery(id+"F0.wireOp",EDGE,"E3")}),-1.0]])]});
            var Q2;
            Q2=makeQuery(id+"F0.imprint","IMPRINT",FACE,{"disambiguationData":[TD([[makeQuery(id+"F0.imprint","IMPRINT",EDGE,{"derivedFrom":sQuery(id+"F0.wireOp",EDGE,"E4")}),-1.0]])]});
            var Q3;
            Q3=makeQuery(id+"F0.imprint","IMPRINT",FACE,{"disambiguationData":[TD([[makeQuery(id+"F0.imprint","IMPRINT",EDGE,{"derivedFrom":sQuery(id+"F0.wireOp",EDGE,"E6")}),-1.0]])]});
            var Q4;
            Q4=makeQuery(id+"F0.imprint","IMPRINT",FACE,{"disambiguationData":[TD([[makeQuery(id+"F0.imprint","IMPRINT",EDGE,{"derivedFrom":sQuery(id+"F0.wireOp",EDGE,"E7")}),-1.0]])]});
            var Q5;
            Q5=makeQuery(id+"F0.imprint","IMPRINT",FACE,{"disambiguationData":[TD([[makeQuery(id+"F0.imprint","IMPRINT",EDGE,{"derivedFrom":sQuery(id+"F0.wireOp",EDGE,"E9")}),-1.0]])]});
            var Q6;
            Q6=makeQuery(id+"F0.imprint","IMPRINT",FACE,{"disambiguationData":[TD([[makeQuery(id+"F0.imprint","IMPRINT",EDGE,{"derivedFrom":sQuery(id+"F0.wireOp",EDGE,"E8")}),-1.0]])]});
            var Q7;
            Q7=makeQuery(id+"F0.imprint","IMPRINT",FACE,{"disambiguationData":[TD([[makeQuery(id+"F0.imprint","IMPRINT",EDGE,{"derivedFrom":sQuery(id+"F0.wireOp",EDGE,"E10")}),-1.0]])]});
            extrude(context, id + "F1", {"entities" : qUnion([Q0, Q1, Q2, Q3, Q4, Q5, Q6, Q7]), "depth" : 10 * mm, "offsetDistance" : 25 * mm});
        }
        {
            var Q0;
            Q0=makeQuery(id+"F1.opExtrude","SWEPT_BODY",BODY,{"disambiguationData":[OSD([sQuery(id+"F0.wireOp",EDGE,"E1"),sQuery(id+"F0.wireOp",EDGE,"E2")])]});
            var Q1;
            Q1=makeQuery(id+"F1.opExtrude","SWEPT_BODY",BODY,{"disambiguationData":[OSD([sQuery(id+"F0.wireOp",EDGE,"E3")])]});
            var Q2;
            Q2=makeQuery(id+"F1.opExtrude","SWEPT_BODY",BODY,{"disambiguationData":[OSD([sQuery(id+"F0.wireOp",EDGE,"E4"),sQuery(id+"F0.wireOp",EDGE,"E5")])]});
            var Q3;
            Q3=makeQuery(id+"F1.opExtrude","SWEPT_BODY",BODY,{"disambiguationData":[OSD([sQuery(id+"F0.wireOp",EDGE,"E6")])]});
            var Q4;
            Q4=makeQuery(id+"F1.opExtrude","SWEPT_BODY",BODY,{"disambiguationData":[OSD([sQuery(id+"F0.wireOp",EDGE,"E7")])]});
            var Q5;
            Q5=makeQuery(id+"F1.opExtrude","SWEPT_BODY",BODY,{"disambiguationData":[OSD([sQuery(id+"F0.wireOp",EDGE,"E8")])]});
            var Q6;
            Q6=makeQuery(id+"F1.opExtrude","SWEPT_BODY",BODY,{"disambiguationData":[OSD([sQuery(id+"F0.wireOp",EDGE,"E9")])]});
            var Q7;
            Q7=makeQuery(id+"F1.opExtrude","SWEPT_BODY",BODY,{"disambiguationData":[OSD([sQuery(id+"F0.wireOp",EDGE,"E10")])]});
            var Q8;
            Q8=qCreatedBy(makeId("Origin.pointOp"),VERTEX);
            transform(context, id + "F2", {"entities" : qUnion([Q0, Q1, Q2, Q3, Q4, Q5, Q6, Q7]), "transformType" : TransformType.SCALE_UNIFORMLY, "scale" : 0.5, "scalePoint" : qUnion([Q8]), "makeCopy" : false});
        }
    });
